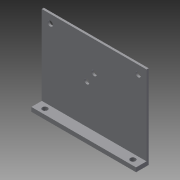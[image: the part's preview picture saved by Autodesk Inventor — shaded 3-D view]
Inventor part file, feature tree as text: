
AUTODESK INVENTOR PART (.ipt)
format: ipt  version: 2015 (Build 190159000, 159)  size: 116,736 bytes
history: native  units: in
note: dims shown in document units (in); Inventor stores cm internally (conversion verified against a paired STEP export)
features: sketch x6, extrude x3, hole x3
ambient origin geometry x8: Origin, YZ Plane, XZ Plane, XY Plane, X Axis, Y Axis, Z Axis, Center Point
bodies: Solid1 (feature_tree)
feature tree (12):
  extrude  "Extrusion1"  Depth=2.5in
  extrude  "Extrusion2"  Depth=0.1in
  hole  "Hole1"  [1 undecoded]
  hole  "Hole2"  [1 undecoded]
  hole  "Hole3"  [1 undecoded]
  extrude  "Extrusion3"  Depth=0.25in
  sketch  "Sketch1"  dims[d0=2.0in d1=2.5in]
  sketch  "Sketch2"  dims[d2=0.05in d3=0.0in d4=0.1in]
  sketch  "Sketch3"  dims[d5=0.25in d6=0.0in d7=0.7in]
  sketch  "Sketch4"  dims[d8=1.25in]
  sketch  "Sketch5"  dims[d9=0.125in d10=0.75in d11=0.375in d12=0.25in d13=0.5635in d14=1.0in d15=0.8108in d16=0.2in]
  sketch  "Sketch6"  dims[d17=0.2in d18=0.2in d19=0.2in d20=0.1254in d21=0.75in d22=0.375in d23=0.25in d24=0.5635in d25=1.0in d26=0.8108in d27=0.125in d28=0.2in d29=0.125in d30=0.2in d31=0.1254in d32=0.75in d33=0.375in d34=0.25in d35=0.5635in d36=1.0in d37=0.8108in d39=0.313in d40=0.313in d42=0.125in d43=1.0in d44=0.0in d47=1.042in]
note: 3 required parameter values undecoded (feature->parameter linkage not recoverable at this tier; creation-order binding heuristic only, values carry confidence <= 0.55)
